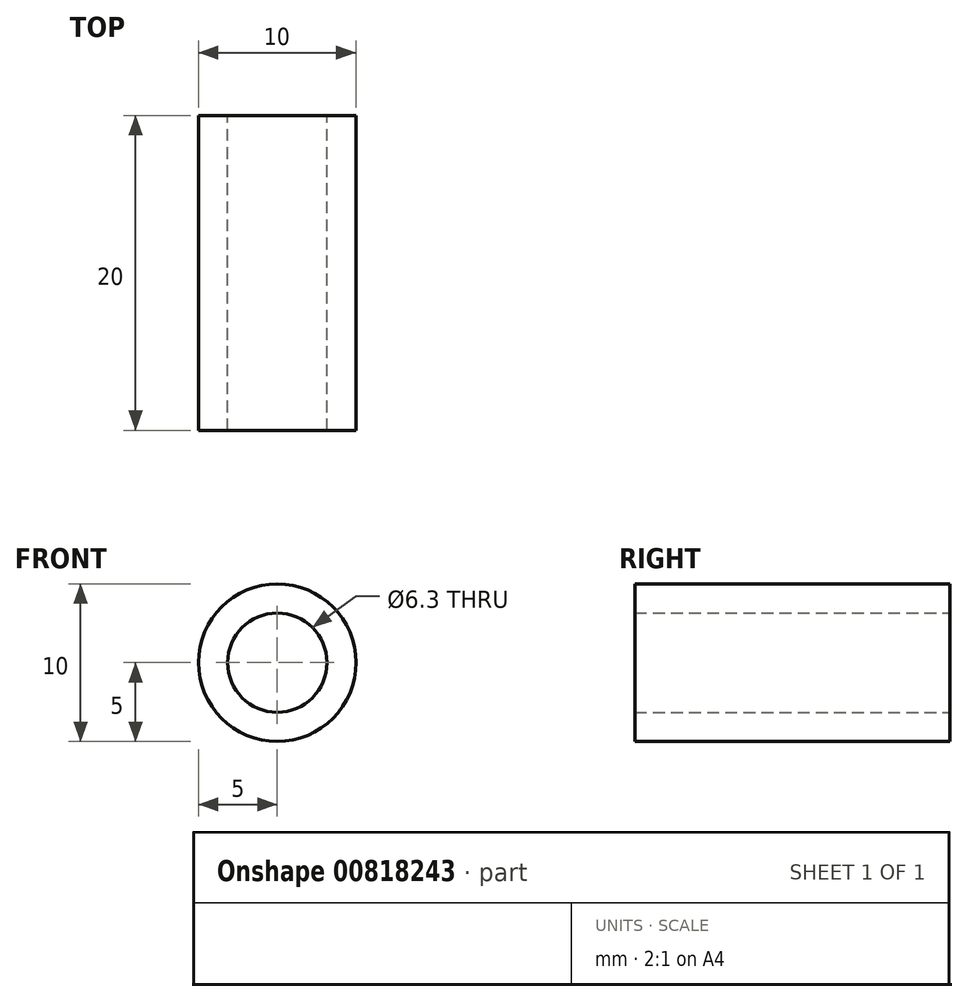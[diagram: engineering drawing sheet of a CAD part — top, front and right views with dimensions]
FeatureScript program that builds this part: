
annotation { "Feature Type Name" : "Feature", "Feature Type Description" : "" }
export const myFeature = defineFeature(function(context is Context, id is Id, definition is map)
    precondition{}
    {
        {
            var Q0;
            Q0=qCreatedBy(makeId("Front.planeOp"),FACE);
            var sketch = newSketch(context, id + "F0", { "sketchPlane" : qUnion([Q0])});
            skCircle(sketch, "E0", {"center": v(0, 0) * mm, "radius": 5 * mm});
            skCircle(sketch, "E1", {"center": v(0, 0) * mm, "radius": 3.15 * mm});
            skSolve(sketch);
        }
        {
            var Q0;
            Q0 = qSketchRegion(id + "F0", true);
            extrude(context, id + "F1", {"entities" : qUnion([Q0]), "depth" : 20 * mm, "offsetDistance" : 25 * mm});
        }
    });
